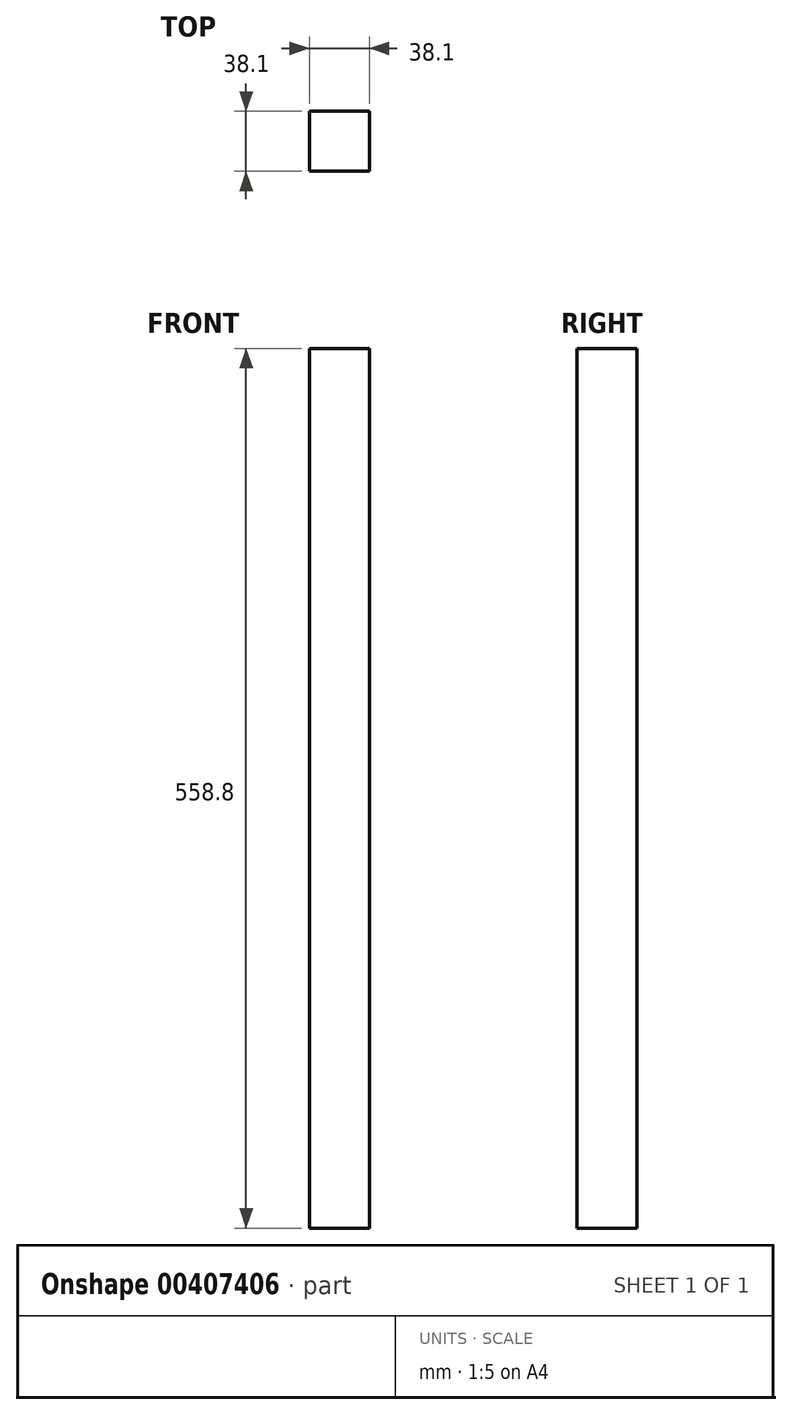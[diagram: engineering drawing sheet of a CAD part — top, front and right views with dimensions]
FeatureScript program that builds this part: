
annotation { "Feature Type Name" : "Feature", "Feature Type Description" : "" }
export const myFeature = defineFeature(function(context is Context, id is Id, definition is map)
    precondition{}
    {
        {
            var Q0;
            Q0=qCreatedBy(makeId("Top.planeOp"),FACE);
            var sketch = newSketch(context, id + "F0", { "sketchPlane" : qUnion([Q0])});
            skLineSegment(sketch, "E0.bottom", {"start": v(19.05, 19.05) * mm, "end": v(-19.05, 19.05) * mm});
            skLineSegment(sketch, "E0.top", {"start": v(19.05, -19.05) * mm, "end": v(-19.05, -19.05) * mm});
            skLineSegment(sketch, "E0.left", {"start": v(19.05, 19.05) * mm, "end": v(19.05, -19.05) * mm});
            skLineSegment(sketch, "E0.right", {"start": v(-19.05, 19.05) * mm, "end": v(-19.05, -19.05) * mm});
            skPoint(sketch, "E0.middle", {"position": v(0, 0) * mm});
            skSolve(sketch);
        }
        {
            var Q0;
            Q0=makeQuery(id+"F0.imprint","IMPRINT",FACE,{"disambiguationData":[TD([[makeQuery(id+"F0.imprint","IMPRINT",EDGE,{"derivedFrom":sQuery(id+"F0.wireOp",EDGE,"E0.bottom")}),1.0]])]});
            extrude(context, id + "F1", {"entities" : qUnion([Q0]), "depth" : 558.8 * mm});
        }
    });
